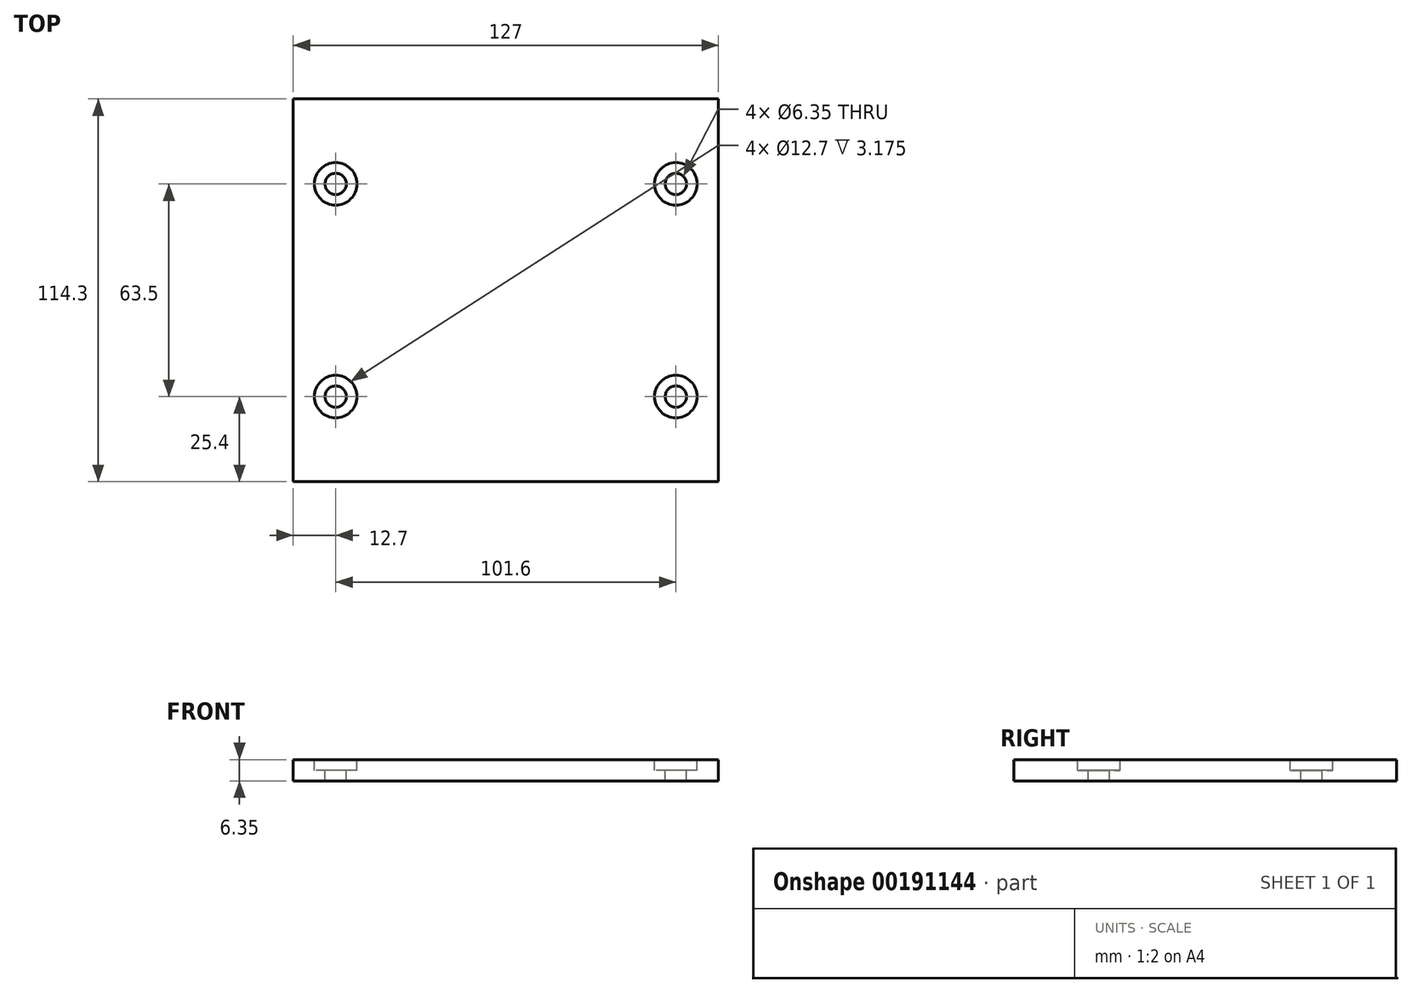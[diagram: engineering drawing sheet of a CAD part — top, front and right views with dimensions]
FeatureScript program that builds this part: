
annotation { "Feature Type Name" : "Feature", "Feature Type Description" : "" }
export const myFeature = defineFeature(function(context is Context, id is Id, definition is map)
    precondition{}
    {
        {
            var Q0;
            Q0=qCreatedBy(makeId("Top.planeOp"),FACE);
            var sketch = newSketch(context, id + "F0", { "sketchPlane" : qUnion([Q0])});
            skLineSegment(sketch, "E0.bottom", {"start": v(-63.5, 57.15) * mm, "end": v(63.5, 57.15) * mm});
            skLineSegment(sketch, "E0.top", {"start": v(-63.5, -57.15) * mm, "end": v(63.5, -57.15) * mm});
            skLineSegment(sketch, "E0.left", {"start": v(-63.5, 57.15) * mm, "end": v(-63.5, -57.15) * mm});
            skLineSegment(sketch, "E0.right", {"start": v(63.5, 57.15) * mm, "end": v(63.5, -57.15) * mm});
            skLineSegment(sketch, "E1", {"start": v(-63.5, -57.15) * mm, "end": v(63.5, 57.15) * mm, "construction": true});
            skPoint(sketch, "E2", {"position": v(0, 0) * mm});
            skSolve(sketch);
        }
        {
            var Q0;
            Q0 = qSketchRegion(id + "F0", true);
            extrude(context, id + "F1", {"entities" : qUnion([Q0]), "depth" : 6.35 * mm});
        }
        {
            var Q0;
            Q0=makeQuery(id+"F1.opExtrude","CAP_FACE",FACE,{"disambiguationData":[OSD([sQuery(id+"F0.wireOp",EDGE,"E0.bottom"),sQuery(id+"F0.wireOp",EDGE,"E0.top"),sQuery(id+"F0.wireOp",EDGE,"E0.left"),sQuery(id+"F0.wireOp",EDGE,"E0.right")])],"isStart":false});
            var sketch = newSketch(context, id + "F2", { "sketchPlane" : qUnion([Q0])});
            skLineSegment(sketch, "E3", {"start": v(-50.8, -57.15) * mm, "end": v(-50.8, 57.15) * mm, "construction": true});
            skLineSegment(sketch, "E4", {"start": v(50.8, -57.15) * mm, "end": v(50.8, 57.15) * mm, "construction": true});
            skPoint(sketch, "E5", {"position": v(-50.8, 31.75) * mm});
            skPoint(sketch, "E6", {"position": v(-50.8, -31.75) * mm});
            skPoint(sketch, "E7", {"position": v(50.8, -31.75) * mm});
            skPoint(sketch, "E8", {"position": v(50.8, 31.75) * mm});
            skSolve(sketch);
        }
        {
            var Q0;
            Q0=sQuery(id+"F2.wireOp",VERTEX,"E6");
            var Q1;
            Q1=sQuery(id+"F2.wireOp",VERTEX,"E5");
            var Q2;
            Q2=sQuery(id+"F2.wireOp",VERTEX,"E7");
            var Q3;
            Q3=sQuery(id+"F2.wireOp",VERTEX,"E8");
            var Q4;
            Q4=makeQuery(id+"F1.opExtrude","SWEPT_BODY",BODY,{"disambiguationData":[OSD([sQuery(id+"F0.wireOp",EDGE,"E0.bottom"),sQuery(id+"F0.wireOp",EDGE,"E0.top"),sQuery(id+"F0.wireOp",EDGE,"E0.left"),sQuery(id+"F0.wireOp",EDGE,"E0.right")])]});
            hole(context, id + "F3", {"style" : HoleStyle.C_BORE, "endStyle" : HoleEndStyle.BLIND, "holeDiameter" : 6.35 * mm, "cBoreDiameter" : 12.7 * mm, "cBoreDepth" : 3.17 * mm, "holeDepth" : 38.1 * mm, "locations" : qUnion([Q0, Q1, Q2, Q3]), "scope" : qUnion([Q4])});
        }
    });
